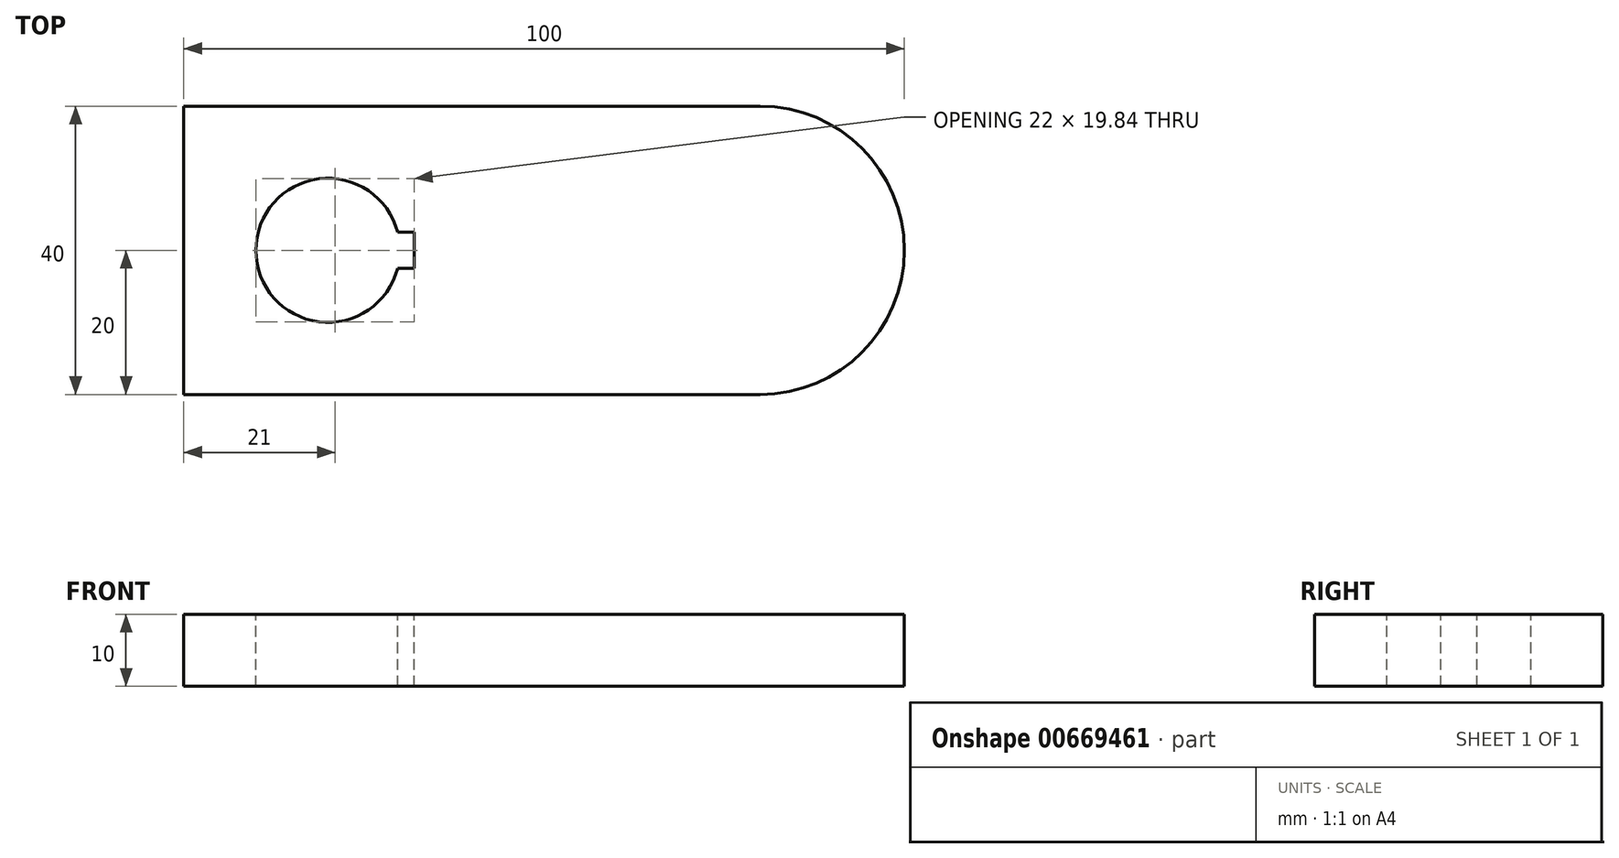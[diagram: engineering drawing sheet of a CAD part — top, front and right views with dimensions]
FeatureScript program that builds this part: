
annotation { "Feature Type Name" : "Feature", "Feature Type Description" : "" }
export const myFeature = defineFeature(function(context is Context, id is Id, definition is map)
    precondition{}
    {
        {
            var Q0;
            Q0=qCreatedBy(makeId("Top.planeOp"),FACE);
            var sketch = newSketch(context, id + "F0", { "sketchPlane" : qUnion([Q0])});
            skLineSegment(sketch, "E0.bottom", {"start": v(0, 0) * mm, "end": v(0, 0) * mm});
            skLineSegment(sketch, "E1", {"start": v(0, 0) * mm, "end": v(0, 40) * mm});
            skLineSegment(sketch, "E2", {"start": v(0, 40) * mm, "end": v(80, 40) * mm});
            skLineSegment(sketch, "E3", {"start": v(80, 0) * mm, "end": v(0, 0) * mm});
            skPoint(sketch, "E4", {"position": v(20, 20) * mm});
            skArc(sketch, "E5", {"start": v(29.68, 22.5) * mm, "mid": v(10, 20) * mm, "end": v(29.68, 17.5) * mm});
            skLineSegment(sketch, "E6.bottom", {"start": v(29.68, 17.5) * mm, "end": v(32, 17.5) * mm});
            skLineSegment(sketch, "E6.top", {"start": v(29.68, 22.5) * mm, "end": v(32, 22.5) * mm});
            skLineSegment(sketch, "E6.right", {"start": v(32, 17.5) * mm, "end": v(32, 22.5) * mm});
            skArc(sketch, "E7", {"start": v(80, 0) * mm, "mid": v(100, 20) * mm, "end": v(80, 40) * mm});
            skSolve(sketch);
        }
        {
            var Q0;
            Q0=makeQuery(id+"F0.imprint","IMPRINT",FACE,{"disambiguationData":[TD([[makeQuery(id+"F0.imprint","IMPRINT",EDGE,{"derivedFrom":sQuery(id+"F0.wireOp",EDGE,"E1")}),-1.0]])]});
            extrude(context, id + "F1", {"entities" : qUnion([Q0]), "oppositeDirection" : true, "depth" : 10 * mm, "offsetDistance" : 25 * mm});
        }
    });
